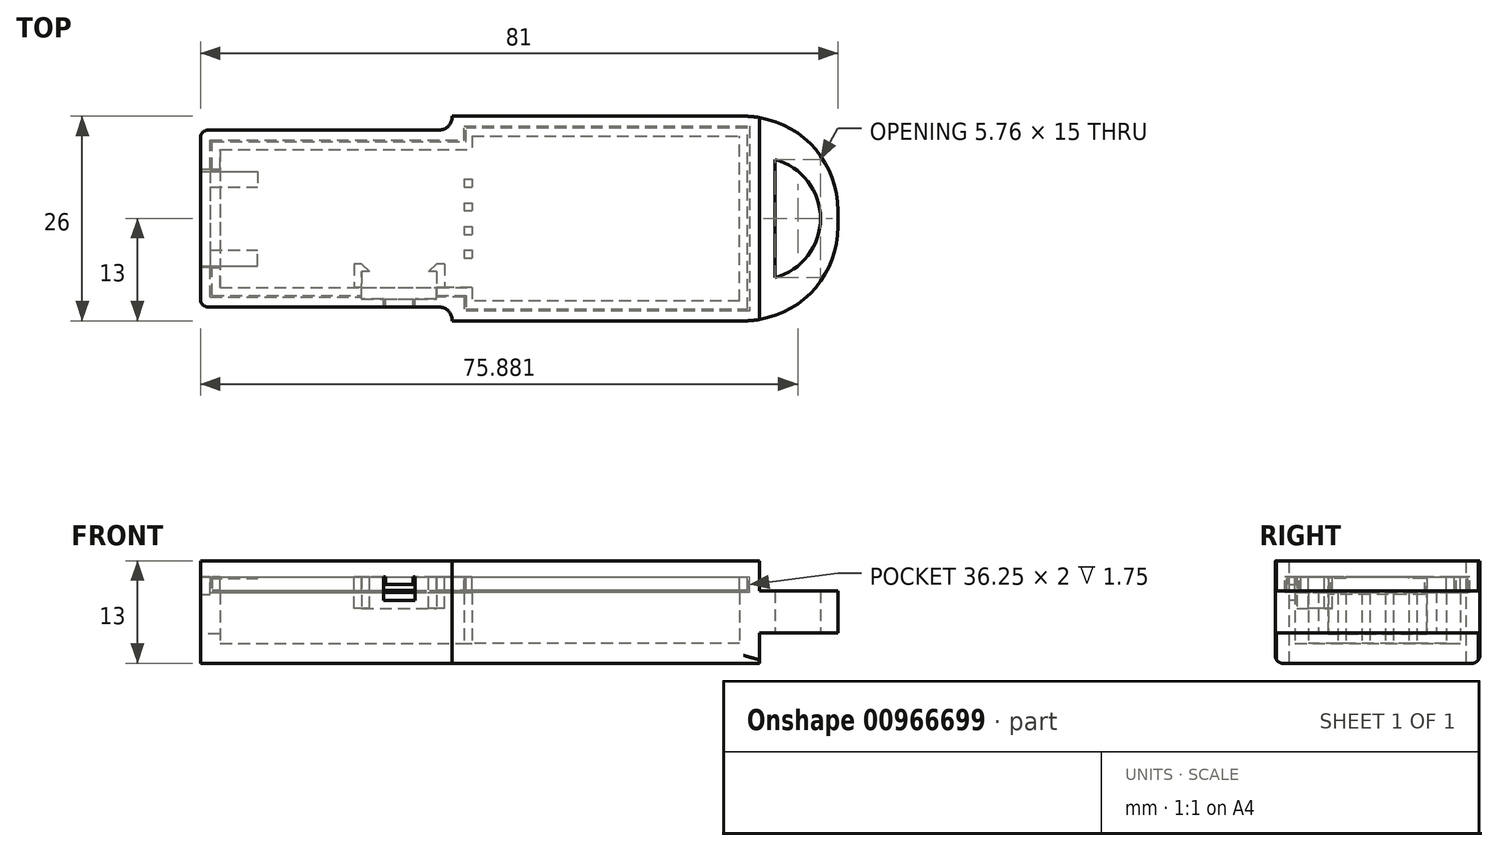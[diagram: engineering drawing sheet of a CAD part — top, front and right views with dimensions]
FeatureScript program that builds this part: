
annotation { "Feature Type Name" : "Feature", "Feature Type Description" : "" }
export const myFeature = defineFeature(function(context is Context, id is Id, definition is map)
    precondition{}
    {
        {
            var Q0;
            Q0=qCreatedBy(makeId("Top.planeOp"),FACE);
            var sketch = newSketch(context, id + "F0", { "sketchPlane" : qUnion([Q0])});
            skLineSegment(sketch, "E0.bottom", {"start": v(-15.5, 8.75) * mm, "end": v(15.5, 8.75) * mm});
            skLineSegment(sketch, "E0.top", {"start": v(-15.5, -8.75) * mm, "end": v(15.5, -8.75) * mm});
            skLineSegment(sketch, "E0.left", {"start": v(-15.5, 8.75) * mm, "end": v(-15.5, -8.75) * mm});
            skLineSegment(sketch, "E0.right", {"start": v(15.5, 8.75) * mm, "end": v(15.5, -8.75) * mm});
            skPoint(sketch, "E0.middle", {"position": v(0, 0) * mm});
            skLineSegment(sketch, "E1.bottom", {"start": v(50.5, -10.5) * mm, "end": v(16.5, -10.5) * mm});
            skLineSegment(sketch, "E1.top", {"start": v(50.5, 10.5) * mm, "end": v(16.5, 10.5) * mm});
            skLineSegment(sketch, "E1.left", {"start": v(50.5, -10.5) * mm, "end": v(50.5, 10.5) * mm});
            skLineSegment(sketch, "E1.right", {"start": v(16.5, -10.5) * mm, "end": v(16.5, 10.5) * mm});
            skPoint(sketch, "E1.middle", {"position": v(33.5, 0) * mm});
            skLineSegment(sketch, "E2.bottom", {"start": v(15.5, 8.75) * mm, "end": v(16.5, 8.75) * mm});
            skLineSegment(sketch, "E2.top", {"start": v(15.5, -8.75) * mm, "end": v(16.5, -8.75) * mm});
            skLineSegment(sketch, "E2.right", {"start": v(16.5, 8.75) * mm, "end": v(16.5, -8.75) * mm});
            skSolve(sketch);
        }
        {
            var Q0;
            Q0 = qSketchRegion(id + "F0", true);
            extrude(context, id + "F1", {"entities" : qUnion([Q0]), "depth" : 8.5 * mm, "offsetDistance" : 25 * mm});
        }
        {
            var Q0;
            Q0=makeQuery(id+"F1.opExtrude","CAP_FACE",FACE,{"disambiguationData":[OSD([sQuery(id+"F0.wireOp",EDGE,"E0.bottom"),sQuery(id+"F0.wireOp",EDGE,"E0.top"),sQuery(id+"F0.wireOp",EDGE,"E0.left"),sQuery(id+"F0.wireOp",EDGE,"E1.bottom"),sQuery(id+"F0.wireOp",EDGE,"E1.top"),sQuery(id+"F0.wireOp",EDGE,"E1.left"),sQuery(id+"F0.wireOp",EDGE,"E1.right")])],"isStart":false});
            shell(context, id + "F2", {"entities" : qUnion([Q0]), "thickness" : 2.5 * mm, "oppositeDirection" : true});
        }
        {
            var Q0;
            Q0=makeQuery(id+"F2.opShell","OFFSET_FACE",FACE,{"disambiguationData":[OSD([sQuery(id+"F0.wireOp",EDGE,"E0.bottom"),sQuery(id+"F0.wireOp",EDGE,"E0.top"),sQuery(id+"F0.wireOp",EDGE,"E0.left"),sQuery(id+"F0.wireOp",EDGE,"E1.bottom"),sQuery(id+"F0.wireOp",EDGE,"E1.top"),sQuery(id+"F0.wireOp",EDGE,"E1.left"),sQuery(id+"F0.wireOp",EDGE,"E1.right"),sQuery(id+"F0.wireOp",EDGE,"E2.bottom"),sQuery(id+"F0.wireOp",EDGE,"E2.top")])]});
            var sketch = newSketch(context, id + "F3", { "sketchPlane" : qUnion([Q0])});
            skLineSegment(sketch, "E3.bottom", {"start": v(15.5, 8) * mm, "end": v(16.5, 8) * mm, "construction": true});
            skLineSegment(sketch, "E3.top", {"start": v(15.5, 7) * mm, "end": v(16.5, 7) * mm, "construction": true});
            skLineSegment(sketch, "E3.left", {"start": v(15.5, 8) * mm, "end": v(15.5, 7) * mm, "construction": true});
            skLineSegment(sketch, "E3.right", {"start": v(16.5, 8) * mm, "end": v(16.5, 7) * mm, "construction": true});
            skLineSegment(sketch, "E4", {"start": v(15.5, 8) * mm, "end": v(15.5, 8.75) * mm, "construction": true});
            skLineSegment(sketch, "E5", {"start": v(15.5, 7) * mm, "end": v(15.5, 5) * mm, "construction": true});
            skLineSegment(sketch, "E6.bottom", {"start": v(15.5, 5) * mm, "end": v(16.5, 5) * mm});
            skLineSegment(sketch, "E6.top", {"start": v(15.5, 4) * mm, "end": v(16.5, 4) * mm});
            skLineSegment(sketch, "E6.left", {"start": v(15.5, 5) * mm, "end": v(15.5, 4) * mm});
            skLineSegment(sketch, "E6.right", {"start": v(16.5, 5) * mm, "end": v(16.5, 4) * mm});
            skLineSegment(sketch, "E7", {"start": v(15.5, 4) * mm, "end": v(15.5, 2) * mm, "construction": true});
            skLineSegment(sketch, "E8.bottom", {"start": v(15.5, 2) * mm, "end": v(16.5, 2) * mm});
            skLineSegment(sketch, "E8.top", {"start": v(15.5, 1) * mm, "end": v(16.5, 1) * mm});
            skLineSegment(sketch, "E8.left", {"start": v(15.5, 2) * mm, "end": v(15.5, 1) * mm});
            skLineSegment(sketch, "E8.right", {"start": v(16.5, 2) * mm, "end": v(16.5, 1) * mm});
            skLineSegment(sketch, "E9", {"start": v(15.5, 1) * mm, "end": v(15.5, -1) * mm, "construction": true});
            skLineSegment(sketch, "E10.bottom", {"start": v(15.5, -1) * mm, "end": v(16.5, -1) * mm});
            skLineSegment(sketch, "E10.top", {"start": v(15.5, -2) * mm, "end": v(16.5, -2) * mm});
            skLineSegment(sketch, "E10.left", {"start": v(15.5, -1) * mm, "end": v(15.5, -2) * mm});
            skLineSegment(sketch, "E10.right", {"start": v(16.5, -1) * mm, "end": v(16.5, -2) * mm});
            skLineSegment(sketch, "E11", {"start": v(15.5, -2) * mm, "end": v(15.5, -4) * mm, "construction": true});
            skLineSegment(sketch, "E12.bottom", {"start": v(15.5, -4) * mm, "end": v(16.5, -4) * mm});
            skLineSegment(sketch, "E12.top", {"start": v(15.5, -5) * mm, "end": v(16.5, -5) * mm});
            skLineSegment(sketch, "E12.left", {"start": v(15.5, -4) * mm, "end": v(15.5, -5) * mm});
            skLineSegment(sketch, "E12.right", {"start": v(16.5, -4) * mm, "end": v(16.5, -5) * mm});
            skLineSegment(sketch, "E13", {"start": v(15.5, -5) * mm, "end": v(15.5, -7) * mm, "construction": true});
            skLineSegment(sketch, "E14.bottom", {"start": v(15.5, -7) * mm, "end": v(16.5, -7) * mm, "construction": true});
            skLineSegment(sketch, "E14.top", {"start": v(15.5, -8) * mm, "end": v(16.5, -8) * mm, "construction": true});
            skLineSegment(sketch, "E14.left", {"start": v(15.5, -7) * mm, "end": v(15.5, -8) * mm, "construction": true});
            skLineSegment(sketch, "E14.right", {"start": v(16.5, -7) * mm, "end": v(16.5, -8) * mm, "construction": true});
            skSolve(sketch);
        }
        {
            var Q0;
            Q0 = qSketchRegion(id + "F3", true);
            extrude(context, id + "F4", {"entities" : qUnion([Q0]), "operationType" : NewBodyOperationType.ADD, "depth" : 6.5 * mm, "offsetDistance" : 25 * mm});
        }
        {
            var Q0;
            Q0=makeQuery(id+"F1.opExtrude","CAP_EDGE",EDGE,{"disambiguationData":[OSD([sQuery(id+"F0.wireOp",EDGE,"E1.bottom")])],"isStart":true});
            var Q1;
            Q1=makeQuery(id+"F1.opExtrude","CAP_EDGE",EDGE,{"disambiguationData":[OSD([sQuery(id+"F0.wireOp",EDGE,"E1.top")])],"isStart":true});
            fillet(context, id + "F5", {"entities" : qUnion([Q0, Q1]), "tangentPropagation" : true, "radius" : 1 * mm, "defaultsChanged" : false, "vertexSettings" : [], "allowEdgeOverflow" : false});
        }
        {
            var Q0;
            Q0=makeQuery(id+"F2.opShell","OFFSET_FACE",FACE,{"disambiguationData":[OSD([sQuery(id+"F0.wireOp",EDGE,"E0.top"),sQuery(id+"F0.wireOp",EDGE,"E2.top")])]});
            var sketch = newSketch(context, id + "F6", { "sketchPlane" : qUnion([Q0])});
            skLineSegment(sketch, "E15.bottom", {"start": v(-2.5, 10.5) * mm, "end": v(-12, 10.5) * mm});
            skLineSegment(sketch, "E15.top", {"start": v(-2.5, 4.5) * mm, "end": v(-12, 4.5) * mm});
            skLineSegment(sketch, "E15.left", {"start": v(-2.5, 10.5) * mm, "end": v(-2.5, 4.5) * mm});
            skLineSegment(sketch, "E15.right", {"start": v(-12, 10.5) * mm, "end": v(-12, 4.5) * mm});
            skLineSegment(sketch, "E16", {"start": v(-2.5, 4.5) * mm, "end": v(-2.5, 0) * mm, "construction": true});
            skLineSegment(sketch, "E17", {"start": v(-12, 4.5) * mm, "end": v(-14, 4.5) * mm, "construction": true});
            skSolve(sketch);
        }
        {
            var Q0;
            Q0=makeQuery(id+"F1.opExtrude","SWEPT_FACE",FACE,{"disambiguationData":[OSD([sQuery(id+"F0.wireOp",EDGE,"E0.top"),sQuery(id+"F0.wireOp",EDGE,"E2.top")])]});
            var sketch = newSketch(context, id + "F7", { "sketchPlane" : qUnion([Q0])});
            skLineSegment(sketch, "E18", {"start": v(7.25, 4.5) * mm, "end": v(7.25, 5.5) * mm, "construction": true});
            skLineSegment(sketch, "E19.bottom", {"start": v(9.25, 5.5) * mm, "end": v(5.25, 5.5) * mm});
            skLineSegment(sketch, "E19.top", {"start": v(9.25, 9.5) * mm, "end": v(5.25, 9.5) * mm});
            skLineSegment(sketch, "E19.left", {"start": v(9.25, 5.5) * mm, "end": v(9.25, 9.5) * mm});
            skLineSegment(sketch, "E19.right", {"start": v(5.25, 5.5) * mm, "end": v(5.25, 9.5) * mm});
            skPoint(sketch, "E19.middle", {"position": v(7.25, 7.5) * mm});
            skSolve(sketch);
        }
        {
            var Q0;
            Q0 = qSketchRegion(id + "F6", true);
            extrude(context, id + "F8", {"entities" : qUnion([Q0]), "operationType" : NewBodyOperationType.REMOVE, "endBound" : BoundingType.SYMMETRIC, "oppositeDirection" : true, "depth" : 3 * mm, "offsetDistance" : 25 * mm});
        }
        {
            var Q0;
            Q0 = qSketchRegion(id + "F7", true);
            extrude(context, id + "F9", {"entities" : qUnion([Q0]), "operationType" : NewBodyOperationType.REMOVE, "endBound" : BoundingType.SYMMETRIC, "oppositeDirection" : true, "depth" : 4 * mm, "offsetDistance" : 25 * mm});
        }
        {
            var Q0;
            {var subQ0=sQuery(id+"F0.wireOp",EDGE,"E1.bottom");var subQ1=sQuery(id+"F0.wireOp",EDGE,"E0.left");var subQ2=sQuery(id+"F0.wireOp",EDGE,"E1.right");var subQ3=sQuery(id+"F0.wireOp",EDGE,"E1.top");var subQ4=sQuery(id+"F0.wireOp",EDGE,"E1.left");var subQ5=sQuery(id+"F0.wireOp",EDGE,"E2.top");var subQ6=sQuery(id+"F0.wireOp",EDGE,"E0.top");var subQ7=sQuery(id+"F0.wireOp",EDGE,"E2.bottom");var subQ8=sQuery(id+"F0.wireOp",EDGE,"E0.bottom");Q0=makeQuery(id+"F9.boolean.opBoolean","SPLIT",FACE,{"disambiguationData":[TD([makeQuery(id+"F1.opExtrude","SWEPT_FACE",FACE,{"disambiguationData":[OSD([subQ0])]})])],"derivedFrom":makeQuery(id+"F1.opExtrude","CAP_FACE",FACE,{"disambiguationData":[OSD([subQ8,subQ6,subQ1,subQ0,subQ3,subQ4,subQ2,subQ7,subQ5])],"isStart":false})});}
            var sketch = newSketch(context, id + "F10", { "sketchPlane" : qUnion([Q0])});
            skLineSegment(sketch, "E20", {"start": v(-15.5, -8.75) * mm, "end": v(-15.5, 8.75) * mm});
            skLineSegment(sketch, "E21", {"start": v(-15.5, 8.75) * mm, "end": v(16.5, 8.75) * mm});
            skLineSegment(sketch, "E22", {"start": v(16.5, 8.75) * mm, "end": v(16.5, 10.5) * mm});
            skLineSegment(sketch, "E23", {"start": v(16.5, 10.5) * mm, "end": v(50.5, 10.5) * mm});
            skLineSegment(sketch, "E24", {"start": v(50.5, 10.5) * mm, "end": v(50.5, -10.5) * mm});
            skLineSegment(sketch, "E25", {"start": v(50.5, -10.5) * mm, "end": v(16.5, -10.5) * mm});
            skLineSegment(sketch, "E26", {"start": v(16.5, -10.5) * mm, "end": v(16.5, -8.75) * mm});
            skLineSegment(sketch, "E27", {"start": v(16.5, -8.75) * mm, "end": v(12, -8.75) * mm});
            skLineSegment(sketch, "E28", {"start": v(2.5, -8.75) * mm, "end": v(-15.5, -8.75) * mm});
            skLineSegment(sketch, "E29", {"start": v(-15.5, 8.75) * mm, "end": v(-16.75, 8.75) * mm, "construction": true});
            skLineSegment(sketch, "E30", {"start": v(-15.5, 8.75) * mm, "end": v(-15.5, 10) * mm, "construction": true});
            skLineSegment(sketch, "E31", {"start": v(-16.75, 8.75) * mm, "end": v(-16.75, 10) * mm});
            skLineSegment(sketch, "E32", {"start": v(-16.75, 10) * mm, "end": v(15.5, 10) * mm});
            skLineSegment(sketch, "E33", {"start": v(16.5, 11.75) * mm, "end": v(50.5, 11.75) * mm});
            skLineSegment(sketch, "E34", {"start": v(50.5, 10.5) * mm, "end": v(50.5, 11.75) * mm, "construction": true});
            skLineSegment(sketch, "E35", {"start": v(50.5, 10.5) * mm, "end": v(51.75, 10.5) * mm, "construction": true});
            skLineSegment(sketch, "E36", {"start": v(50.5, 11.75) * mm, "end": v(51.75, 11.75) * mm});
            skLineSegment(sketch, "E37", {"start": v(51.75, 11.75) * mm, "end": v(51.75, 10.5) * mm});
            skLineSegment(sketch, "E38", {"start": v(50.5, -10.5) * mm, "end": v(51.75, -10.5) * mm, "construction": true});
            skLineSegment(sketch, "E39", {"start": v(50.5, -10.5) * mm, "end": v(50.5, -11.75) * mm, "construction": true});
            skLineSegment(sketch, "E40", {"start": v(51.75, 10.5) * mm, "end": v(51.75, -11.75) * mm});
            skLineSegment(sketch, "E41", {"start": v(16.5, -11.75) * mm, "end": v(51.75, -11.75) * mm});
            skLineSegment(sketch, "E42", {"start": v(-16.75, 10) * mm, "end": v(-16.75, -10) * mm});
            skLineSegment(sketch, "E43", {"start": v(-15.5, -8.75) * mm, "end": v(-15.5, -10) * mm, "construction": true});
            skLineSegment(sketch, "E44", {"start": v(-16.75, -10) * mm, "end": v(2.5, -10) * mm});
            skLineSegment(sketch, "E45", {"start": v(15.5, 10) * mm, "end": v(15.5, 8.75) * mm});
            skLineSegment(sketch, "E46", {"start": v(15.5, 10) * mm, "end": v(15.5, 11.75) * mm});
            skLineSegment(sketch, "E47", {"start": v(15.5, 11.75) * mm, "end": v(16.5, 11.75) * mm});
            skLineSegment(sketch, "E48", {"start": v(16.5, -11.75) * mm, "end": v(15.5, -11.75) * mm});
            skLineSegment(sketch, "E49", {"start": v(15.5, -10) * mm, "end": v(15.5, -11.75) * mm});
            skLineSegment(sketch, "E50", {"start": v(15.5, -10) * mm, "end": v(12, -10) * mm});
            skLineSegment(sketch, "E51", {"start": v(12, -8.75) * mm, "end": v(12, -8.75) * mm});
            skLineSegment(sketch, "E52", {"start": v(12, -10) * mm, "end": v(12, -8.75) * mm});
            skLineSegment(sketch, "E53", {"start": v(2.5, -8.75) * mm, "end": v(2.5, -8.75) * mm});
            skLineSegment(sketch, "E54", {"start": v(2.5, -8.75) * mm, "end": v(2.5, -10) * mm});
            skSolve(sketch);
        }
        {
            var Q0;
            Q0 = qSketchRegion(id + "F10", true);
            extrude(context, id + "F11", {"entities" : qUnion([Q0]), "operationType" : NewBodyOperationType.REMOVE, "oppositeDirection" : true, "depth" : 2 * mm, "offsetDistance" : 25 * mm});
        }
        {
            var Q0;
            {var subQ0=sQuery(id+"F0.wireOp",EDGE,"E1.bottom");var subQ1=sQuery(id+"F0.wireOp",EDGE,"E0.left");var subQ2=sQuery(id+"F0.wireOp",EDGE,"E1.left");var subQ3=sQuery(id+"F0.wireOp",EDGE,"E2.top");var subQ4=sQuery(id+"F0.wireOp",EDGE,"E0.top");var subQ5=sQuery(id+"F0.wireOp",EDGE,"E1.top");var subQ6=sQuery(id+"F0.wireOp",EDGE,"E2.bottom");var subQ7=sQuery(id+"F0.wireOp",EDGE,"E0.bottom");var subQ8=sQuery(id+"F0.wireOp",EDGE,"E1.right");Q0=makeQuery(id+"F9.boolean.opBoolean","SPLIT",FACE,{"disambiguationData":[TD([makeQuery(id+"F1.opExtrude","SWEPT_FACE",FACE,{"disambiguationData":[OSD([subQ0])]})])],"derivedFrom":makeQuery(id+"F1.opExtrude","CAP_FACE",FACE,{"disambiguationData":[OSD([subQ7,subQ4,subQ1,subQ0,subQ5,subQ2,subQ8,subQ6,subQ3])],"isStart":false})});}
            var sketch = newSketch(context, id + "F12", { "sketchPlane" : qUnion([Q0])});
            skLineSegment(sketch, "E55", {"start": v(-18, 11.25) * mm, "end": v(14, 11.25) * mm});
            skLineSegment(sketch, "E56", {"start": v(14, 11.25) * mm, "end": v(14, 13) * mm});
            skLineSegment(sketch, "E57", {"start": v(14, 13) * mm, "end": v(53, 13) * mm});
            skLineSegment(sketch, "E58", {"start": v(53, 13) * mm, "end": v(53, -13) * mm});
            skLineSegment(sketch, "E59", {"start": v(53, -13) * mm, "end": v(14, -13) * mm});
            skLineSegment(sketch, "E60", {"start": v(14, -13) * mm, "end": v(14, -11.25) * mm});
            skLineSegment(sketch, "E61", {"start": v(14, -11.25) * mm, "end": v(-18, -11.25) * mm});
            skLineSegment(sketch, "E62", {"start": v(-18, -11.25) * mm, "end": v(-18, 11.25) * mm});
            skSolve(sketch);
        }
        {
            var Q0;
            Q0 = qSketchRegion(id + "F12", true);
            extrude(context, id + "F13", {"entities" : qUnion([Q0]), "depth" : 2 * mm, "offsetDistance" : 25 * mm});
        }
        {
            var Q0;
            Q0=makeQuery(id+"F1.opExtrude","SWEPT_EDGE",EDGE,{"disambiguationData":[OSD([sQuery(id+"F0.wireOp",EDGE,"E0.bottom"),sQuery(id+"F0.wireOp",EDGE,"E0.left")])]});
            var Q1;
            Q1=makeQuery(id+"F1.opExtrude","SWEPT_EDGE",EDGE,{"disambiguationData":[OSD([sQuery(id+"F0.wireOp",EDGE,"E0.top"),sQuery(id+"F0.wireOp",EDGE,"E0.left")])]});
            var Q2;
            Q2=makeQuery(id+"F13.opExtrude","SWEPT_EDGE",EDGE,{"disambiguationData":[OSD([sQuery(id+"F12.wireOp",EDGE,"E55"),sQuery(id+"F12.wireOp",EDGE,"E62")])]});
            var Q3;
            Q3=makeQuery(id+"F13.opExtrude","SWEPT_EDGE",EDGE,{"disambiguationData":[OSD([sQuery(id+"F12.wireOp",EDGE,"E61"),sQuery(id+"F12.wireOp",EDGE,"E62")])]});
            fillet(context, id + "F14", {"entities" : qUnion([Q0, Q1, Q2, Q3]), "tangentPropagation" : true, "radius" : 1 * mm, "defaultsChanged" : false, "vertexSettings" : [], "allowEdgeOverflow" : false});
        }
        {
            var Q0;
            Q0=makeQuery(id+"F1.opExtrude","SWEPT_EDGE",EDGE,{"disambiguationData":[OSD([sQuery(id+"F0.wireOp",EDGE,"E1.right"),sQuery(id+"F0.wireOp",EDGE,"E2.top"),sQuery(id+"F0.wireOp",EDGE,"E2.right")])]});
            var Q1;
            Q1=makeQuery(id+"F13.opExtrude","SWEPT_EDGE",EDGE,{"disambiguationData":[OSD([sQuery(id+"F12.wireOp",EDGE,"E60"),sQuery(id+"F12.wireOp",EDGE,"E61")])]});
            var Q2;
            Q2=makeQuery(id+"F1.opExtrude","SWEPT_EDGE",EDGE,{"disambiguationData":[OSD([sQuery(id+"F0.wireOp",EDGE,"E1.right"),sQuery(id+"F0.wireOp",EDGE,"E2.bottom"),sQuery(id+"F0.wireOp",EDGE,"E2.right")])]});
            var Q3;
            Q3=makeQuery(id+"F13.opExtrude","SWEPT_EDGE",EDGE,{"disambiguationData":[OSD([sQuery(id+"F12.wireOp",EDGE,"E55"),sQuery(id+"F12.wireOp",EDGE,"E56")])]});
            fillet(context, id + "F15", {"entities" : qUnion([Q0, Q1, Q2, Q3]), "tangentPropagation" : true, "radius" : 1.7 * mm, "defaultsChanged" : true, "vertexSettings" : [], "allowEdgeOverflow" : false});
        }
        {
            var Q0;
            Q0=makeQuery(id+"F13.opExtrude","CAP_FACE",FACE,{"disambiguationData":[OSD([sQuery(id+"F12.wireOp",EDGE,"E55"),sQuery(id+"F12.wireOp",EDGE,"E56"),sQuery(id+"F12.wireOp",EDGE,"E57"),sQuery(id+"F12.wireOp",EDGE,"E58"),sQuery(id+"F12.wireOp",EDGE,"E59"),sQuery(id+"F12.wireOp",EDGE,"E60"),sQuery(id+"F12.wireOp",EDGE,"E61"),sQuery(id+"F12.wireOp",EDGE,"E62")])],"isStart":true});
            var sketch = newSketch(context, id + "F16", { "sketchPlane" : qUnion([Q0])});
            skLineSegment(sketch, "E63", {"start": v(-15.5, -8.75) * mm, "end": v(16.5, -8.75) * mm});
            skLineSegment(sketch, "E64", {"start": v(16.5, -10.5) * mm, "end": v(16.5, -8.75) * mm});
            skLineSegment(sketch, "E65", {"start": v(16.5, -10.5) * mm, "end": v(50.5, -10.5) * mm});
            skLineSegment(sketch, "E66", {"start": v(50.5, 10.5) * mm, "end": v(50.5, -10.5) * mm});
            skLineSegment(sketch, "E67", {"start": v(50.5, 10.5) * mm, "end": v(16.5, 10.5) * mm});
            skLineSegment(sketch, "E68", {"start": v(16.5, 8.75) * mm, "end": v(16.5, 10.5) * mm});
            skLineSegment(sketch, "E69", {"start": v(16.5, 8.75) * mm, "end": v(12, 8.75) * mm});
            skLineSegment(sketch, "E70", {"start": v(-15.5, 8.75) * mm, "end": v(-15.5, -8.75) * mm});
            skLineSegment(sketch, "E71", {"start": v(-15.5, 8.75) * mm, "end": v(2.5, 8.75) * mm});
            skLineSegment(sketch, "E72", {"start": v(-15.5, 8.75) * mm, "end": v(-16.5, 8.75) * mm, "construction": true});
            skLineSegment(sketch, "E73", {"start": v(-15.5, 8.75) * mm, "end": v(-15.5, 9.75) * mm, "construction": true});
            skLineSegment(sketch, "E74", {"start": v(-16.5, 9.75) * mm, "end": v(-16.5, -9.75) * mm});
            skLineSegment(sketch, "E75", {"start": v(-16.5, 9.75) * mm, "end": v(2.5, 9.75) * mm});
            skLineSegment(sketch, "E76", {"start": v(2.5, 9.75) * mm, "end": v(2.5, 8.75) * mm});
            skLineSegment(sketch, "E77", {"start": v(12, 8.75) * mm, "end": v(12, 9.75) * mm});
            skLineSegment(sketch, "E78", {"start": v(16.5, 10.5) * mm, "end": v(16.5, 11.5) * mm, "construction": true});
            skLineSegment(sketch, "E79", {"start": v(16.5, 11.5) * mm, "end": v(51.5, 11.5) * mm});
            skLineSegment(sketch, "E80", {"start": v(50.5, 10.5) * mm, "end": v(51.5, 10.5) * mm, "construction": true});
            skLineSegment(sketch, "E81", {"start": v(51.5, 11.5) * mm, "end": v(51.5, -11.5) * mm});
            skLineSegment(sketch, "E82", {"start": v(50.5, -10.5) * mm, "end": v(50.5, -11.5) * mm, "construction": true});
            skLineSegment(sketch, "E83", {"start": v(51.5, -11.5) * mm, "end": v(15.75, -11.5) * mm});
            skLineSegment(sketch, "E84", {"start": v(-16.5, -9.75) * mm, "end": v(15.75, -9.75) * mm});
            skLineSegment(sketch, "E85", {"start": v(12, 9.75) * mm, "end": v(15.75, 9.75) * mm});
            skLineSegment(sketch, "E86", {"start": v(15.75, 11.5) * mm, "end": v(16.5, 11.5) * mm});
            skLineSegment(sketch, "E87", {"start": v(-15.5, -8.75) * mm, "end": v(-15.5, -9.75) * mm});
            skLineSegment(sketch, "E88", {"start": v(15.75, 9.75) * mm, "end": v(15.75, 11.5) * mm});
            skLineSegment(sketch, "E89", {"start": v(15.5, -10) * mm, "end": v(15.75, -10) * mm, "construction": true});
            skLineSegment(sketch, "E90", {"start": v(15.75, -9.75) * mm, "end": v(15.75, -11.5) * mm});
            skSolve(sketch);
        }
        {
            var Q0;
            Q0 = qSketchRegion(id + "F16", true);
            extrude(context, id + "F17", {"entities" : qUnion([Q0]), "operationType" : NewBodyOperationType.ADD, "depth" : 1.75 * mm, "offsetDistance" : 25 * mm});
        }
        {
            var Q0;
            Q0=makeQuery(id+"F1.opExtrude","SWEPT_FACE",FACE,{"disambiguationData":[OSD([sQuery(id+"F0.wireOp",EDGE,"E0.left")])]});
            var sketch = newSketch(context, id + "F18", { "sketchPlane" : qUnion([Q0])});
            skLineSegment(sketch, "E91.bottom", {"start": v(6.25, 1.25) * mm, "end": v(-6.25, 1.25) * mm});
            skLineSegment(sketch, "E91.top", {"start": v(6.25, 8.5) * mm, "end": v(-6.25, 8.5) * mm});
            skLineSegment(sketch, "E91.left", {"start": v(6.25, 1.25) * mm, "end": v(6.25, 8.5) * mm});
            skLineSegment(sketch, "E91.right", {"start": v(-6.25, 1.25) * mm, "end": v(-6.25, 8.5) * mm});
            skPoint(sketch, "E91.middle", {"position": v(0, 4.88) * mm});
            skLineSegment(sketch, "E92", {"start": v(0, 1.25) * mm, "end": v(0, 0) * mm, "construction": true});
            skSolve(sketch);
        }
        {
            var Q0;
            Q0 = qSketchRegion(id + "F18", true);
            extrude(context, id + "F19", {"entities" : qUnion([Q0]), "operationType" : NewBodyOperationType.REMOVE, "oppositeDirection" : true, "depth" : 3 * mm, "offsetDistance" : 25 * mm});
        }
        {
            var Q0;
            {var subQ24=sQuery(id+"F10.wireOp",EDGE,"E32");Q0=makeQuery(id+"F10.imprint","IMPRINT",FACE,{"disambiguationData":[TD([[makeQuery(id+"F10.imprint","IMPRINT",EDGE,{"derivedFrom":subQ24}),1.0]])]});}
            var sketch = newSketch(context, id + "F20", { "sketchPlane" : qUnion([Q0])});
            skLineSegment(sketch, "E93.bottom", {"start": v(-18, 6) * mm, "end": v(-16.75, 6) * mm});
            skLineSegment(sketch, "E93.top", {"start": v(-18, -6) * mm, "end": v(-16.75, -6) * mm});
            skLineSegment(sketch, "E93.left", {"start": v(-18, 6) * mm, "end": v(-18, -6) * mm});
            skLineSegment(sketch, "E93.right", {"start": v(-16.75, 6) * mm, "end": v(-16.75, -6) * mm});
            skLineSegment(sketch, "E94", {"start": v(-18, 6.25) * mm, "end": v(-18, 6) * mm, "construction": true});
            skLineSegment(sketch, "E95", {"start": v(-18, -6) * mm, "end": v(-18, -6.25) * mm, "construction": true});
            skSolve(sketch);
        }
        {
            var Q0;
            Q0 = qSketchRegion(id + "F20", true);
            extrude(context, id + "F21", {"entities" : qUnion([Q0]), "operationType" : NewBodyOperationType.ADD, "oppositeDirection" : true, "depth" : 2.25 * mm, "offsetDistance" : 25 * mm});
        }
        {
            var Q0;
            Q0=makeQuery(id+"F19.boolean.opBoolean","MERGE",FACE,{"derivedFrom":[makeQuery(id+"F13.opExtrude","CAP_FACE",FACE,{"disambiguationData":[OSD([sQuery(id+"F12.wireOp",EDGE,"E55"),sQuery(id+"F12.wireOp",EDGE,"E56"),sQuery(id+"F12.wireOp",EDGE,"E57"),sQuery(id+"F12.wireOp",EDGE,"E58"),sQuery(id+"F12.wireOp",EDGE,"E59"),sQuery(id+"F12.wireOp",EDGE,"E60"),sQuery(id+"F12.wireOp",EDGE,"E61"),sQuery(id+"F12.wireOp",EDGE,"E62")])],"isStart":true})],"fromTools":[makeQuery(id+"F19.opExtrude","SWEPT_FACE",FACE,{"disambiguationData":[OSD([sQuery(id+"F18.wireOp",EDGE,"E91.top")])]})]});
            var sketch = newSketch(context, id + "F22", { "sketchPlane" : qUnion([Q0])});
            skLineSegment(sketch, "E96", {"start": v(5.5, 11.25) * mm, "end": v(5.5, 10.25) * mm});
            skLineSegment(sketch, "E97", {"start": v(5.25, 11.25) * mm, "end": v(5.5, 11.25) * mm, "construction": true});
            skLineSegment(sketch, "E98", {"start": v(5.5, 11.25) * mm, "end": v(9, 11.25) * mm});
            skLineSegment(sketch, "E99", {"start": v(9.25, 11.25) * mm, "end": v(9, 11.25) * mm, "construction": true});
            skLineSegment(sketch, "E100", {"start": v(9, 11.25) * mm, "end": v(9, 10.25) * mm});
            skLineSegment(sketch, "E101", {"start": v(5.5, 10.25) * mm, "end": v(9, 10.25) * mm});
            skSolve(sketch);
        }
        {
            var Q0;
            Q0 = qSketchRegion(id + "F22", true);
            extrude(context, id + "F23", {"entities" : qUnion([Q0]), "operationType" : NewBodyOperationType.ADD, "depth" : 1 * mm, "offsetDistance" : 25 * mm});
        }
        {
            var Q0;
            Q0=makeQuery(id+"F17.opExtrude","SWEPT_FACE",FACE,{"disambiguationData":[OSD([sQuery(id+"F16.wireOp",EDGE,"E69")])]});
            var sketch = newSketch(context, id + "F24", { "sketchPlane" : qUnion([Q0])});
            skLineSegment(sketch, "E102.bottom", {"start": v(-2.5, 4.5) * mm, "end": v(-1.5, 4.5) * mm});
            skLineSegment(sketch, "E102.top", {"start": v(-2.5, 8.5) * mm, "end": v(-1.5, 8.5) * mm});
            skLineSegment(sketch, "E102.left", {"start": v(-2.5, 4.5) * mm, "end": v(-2.5, 8.5) * mm});
            skLineSegment(sketch, "E102.right", {"start": v(-1.5, 4.5) * mm, "end": v(-1.5, 8.5) * mm});
            skLineSegment(sketch, "E103.bottom", {"start": v(-13, 4.5) * mm, "end": v(-12, 4.5) * mm});
            skLineSegment(sketch, "E103.top", {"start": v(-13, 8.5) * mm, "end": v(-12, 8.5) * mm});
            skLineSegment(sketch, "E103.left", {"start": v(-13, 4.5) * mm, "end": v(-13, 8.5) * mm});
            skLineSegment(sketch, "E103.right", {"start": v(-12, 4.5) * mm, "end": v(-12, 8.5) * mm});
            skSolve(sketch);
        }
        {
            var Q0;
            Q0 = qSketchRegion(id + "F24", true);
            extrude(context, id + "F25", {"entities" : qUnion([Q0]), "operationType" : NewBodyOperationType.ADD, "depth" : 2 * mm, "offsetDistance" : 25 * mm});
        }
        {
            var Q0;
            Q0=makeQuery(id+"F25.opExtrude","CAP_FACE",FACE,{"disambiguationData":[OSD([sQuery(id+"F24.wireOp",EDGE,"E102.bottom"),sQuery(id+"F24.wireOp",EDGE,"E102.top"),sQuery(id+"F24.wireOp",EDGE,"E102.left"),sQuery(id+"F24.wireOp",EDGE,"E102.right")])],"isStart":false});
            var sketch = newSketch(context, id + "F26", { "sketchPlane" : qUnion([Q0])});
            skLineSegment(sketch, "E104.bottom", {"start": v(-1.5, 4.5) * mm, "end": v(-3.5, 4.5) * mm});
            skLineSegment(sketch, "E104.top", {"start": v(-1.5, 8.5) * mm, "end": v(-3.5, 8.5) * mm});
            skLineSegment(sketch, "E104.left", {"start": v(-1.5, 4.5) * mm, "end": v(-1.5, 8.5) * mm});
            skLineSegment(sketch, "E104.right", {"start": v(-3.5, 4.5) * mm, "end": v(-3.5, 8.5) * mm});
            skLineSegment(sketch, "E105.bottom", {"start": v(-13, 4.5) * mm, "end": v(-11, 4.5) * mm});
            skLineSegment(sketch, "E105.top", {"start": v(-13, 8.5) * mm, "end": v(-11, 8.5) * mm});
            skLineSegment(sketch, "E105.left", {"start": v(-13, 4.5) * mm, "end": v(-13, 8.5) * mm});
            skLineSegment(sketch, "E105.right", {"start": v(-11, 4.5) * mm, "end": v(-11, 8.5) * mm});
            skSolve(sketch);
        }
        {
            var Q0;
            Q0 = qSketchRegion(id + "F26", true);
            extrude(context, id + "F27", {"entities" : qUnion([Q0]), "operationType" : NewBodyOperationType.ADD, "depth" : 1 * mm, "offsetDistance" : 25 * mm});
        }
        {
            var Q0;
            Q0=makeQuery(id+"F27.opExtrude","CAP_EDGE",EDGE,{"disambiguationData":[OSD([sQuery(id+"F26.wireOp",EDGE,"E104.right")])],"isStart":false});
            var Q1;
            Q1=makeQuery(id+"F27.opExtrude","CAP_EDGE",EDGE,{"disambiguationData":[OSD([sQuery(id+"F26.wireOp",EDGE,"E105.right")])],"isStart":false});
            chamfer(context, id + "F28", {"entities" : qUnion([Q0, Q1]), "width" : 1 * mm, "tangentPropagation" : true});
        }
        {
            var Q0;
            Q0=makeQuery(id+"F19.boolean.opBoolean","MERGE",FACE,{"derivedFrom":[makeQuery(id+"F13.opExtrude","CAP_FACE",FACE,{"disambiguationData":[OSD([sQuery(id+"F12.wireOp",EDGE,"E55"),sQuery(id+"F12.wireOp",EDGE,"E56"),sQuery(id+"F12.wireOp",EDGE,"E57"),sQuery(id+"F12.wireOp",EDGE,"E58"),sQuery(id+"F12.wireOp",EDGE,"E59"),sQuery(id+"F12.wireOp",EDGE,"E60"),sQuery(id+"F12.wireOp",EDGE,"E61"),sQuery(id+"F12.wireOp",EDGE,"E62")])],"isStart":true})],"fromTools":[makeQuery(id+"F19.opExtrude","SWEPT_FACE",FACE,{"disambiguationData":[OSD([sQuery(id+"F18.wireOp",EDGE,"E91.top")])]})]});
            var sketch = newSketch(context, id + "F29", { "sketchPlane" : qUnion([Q0])});
            skLineSegment(sketch, "E106.bottom", {"start": v(-16.75, -6) * mm, "end": v(-10.75, -6) * mm});
            skLineSegment(sketch, "E106.top", {"start": v(-16.75, -4) * mm, "end": v(-10.75, -4) * mm});
            skLineSegment(sketch, "E106.left", {"start": v(-16.75, -6) * mm, "end": v(-16.75, -4) * mm});
            skLineSegment(sketch, "E106.right", {"start": v(-10.75, -6) * mm, "end": v(-10.75, -4) * mm});
            skLineSegment(sketch, "E107.bottom", {"start": v(-16.75, 6) * mm, "end": v(-10.75, 6) * mm});
            skLineSegment(sketch, "E107.top", {"start": v(-16.75, 4) * mm, "end": v(-10.75, 4) * mm});
            skLineSegment(sketch, "E107.left", {"start": v(-16.75, 6) * mm, "end": v(-16.75, 4) * mm});
            skLineSegment(sketch, "E107.right", {"start": v(-10.75, 6) * mm, "end": v(-10.75, 4) * mm});
            skSolve(sketch);
        }
        {
            var Q0;
            Q0 = qSketchRegion(id + "F29", true);
            extrude(context, id + "F30", {"entities" : qUnion([Q0]), "operationType" : NewBodyOperationType.ADD, "depth" : 0.25 * mm, "offsetDistance" : 25 * mm});
        }
        {
            var Q0;
            Q0=makeQuery(id+"F1.opExtrude","SWEPT_FACE",FACE,{"disambiguationData":[OSD([sQuery(id+"F0.wireOp",EDGE,"E1.left")])]});
            var sketch = newSketch(context, id + "F31", { "sketchPlane" : qUnion([Q0])});
            skLineSegment(sketch, "E108.bottom", {"start": v(13, 1.33) * mm, "end": v(-13, 1.33) * mm});
            skLineSegment(sketch, "E108.top", {"start": v(13, 6.67) * mm, "end": v(-13, 6.67) * mm});
            skLineSegment(sketch, "E108.left", {"start": v(13, 1.33) * mm, "end": v(13, 6.67) * mm});
            skLineSegment(sketch, "E108.right", {"start": v(-13, 1.33) * mm, "end": v(-13, 6.67) * mm});
            skPoint(sketch, "E108.middle", {"position": v(0, 4) * mm});
            skLineSegment(sketch, "E109", {"start": v(0, 8.5) * mm, "end": v(0, 4) * mm});
            skSolve(sketch);
        }
        {
            var Q0;
            Q0 = qSketchRegion(id + "F31", true);
            extrude(context, id + "F32", {"entities" : qUnion([Q0]), "operationType" : NewBodyOperationType.ADD, "depth" : 10 * mm, "offsetDistance" : 25 * mm});
        }
        {
            var Q0;
            Q0=makeQuery(id+"F32.opExtrude","CAP_EDGE",EDGE,{"disambiguationData":[OSD([sQuery(id+"F31.wireOp",EDGE,"E108.right")])],"isStart":false});
            var Q1;
            Q1=makeQuery(id+"F32.opExtrude","CAP_EDGE",EDGE,{"disambiguationData":[OSD([sQuery(id+"F31.wireOp",EDGE,"E108.left")])],"isStart":false});
            fillet(context, id + "F33", {"entities" : qUnion([Q0, Q1]), "tangentPropagation" : true, "radius" : 12 * mm, "defaultsChanged" : false, "vertexSettings" : [], "allowEdgeOverflow" : false});
        }
        {
            var Q0;
            Q0=makeQuery(id+"F32.opExtrude","SWEPT_FACE",FACE,{"disambiguationData":[OSD([sQuery(id+"F31.wireOp",EDGE,"E108.top")])]});
            var sketch = newSketch(context, id + "F34", { "sketchPlane" : qUnion([Q0])});
            skLineSegment(sketch, "E110.right", {"start": v(55, -7.5) * mm, "end": v(55, 7.5) * mm});
            skArc(sketch, "E111", {"start": v(55, -7.5) * mm, "mid": v(60.76, 0) * mm, "end": v(55, 7.5) * mm});
            skLineSegment(sketch, "E112", {"start": v(53, 0) * mm, "end": v(55, 0) * mm});
            skSolve(sketch);
        }
        {
            var Q0;
            Q0 = qSketchRegion(id + "F34", true);
            extrude(context, id + "F35", {"entities" : qUnion([Q0]), "operationType" : NewBodyOperationType.REMOVE, "endBound" : BoundingType.SYMMETRIC, "depth" : 20 * mm, "offsetDistance" : 25 * mm});
        }
    });
